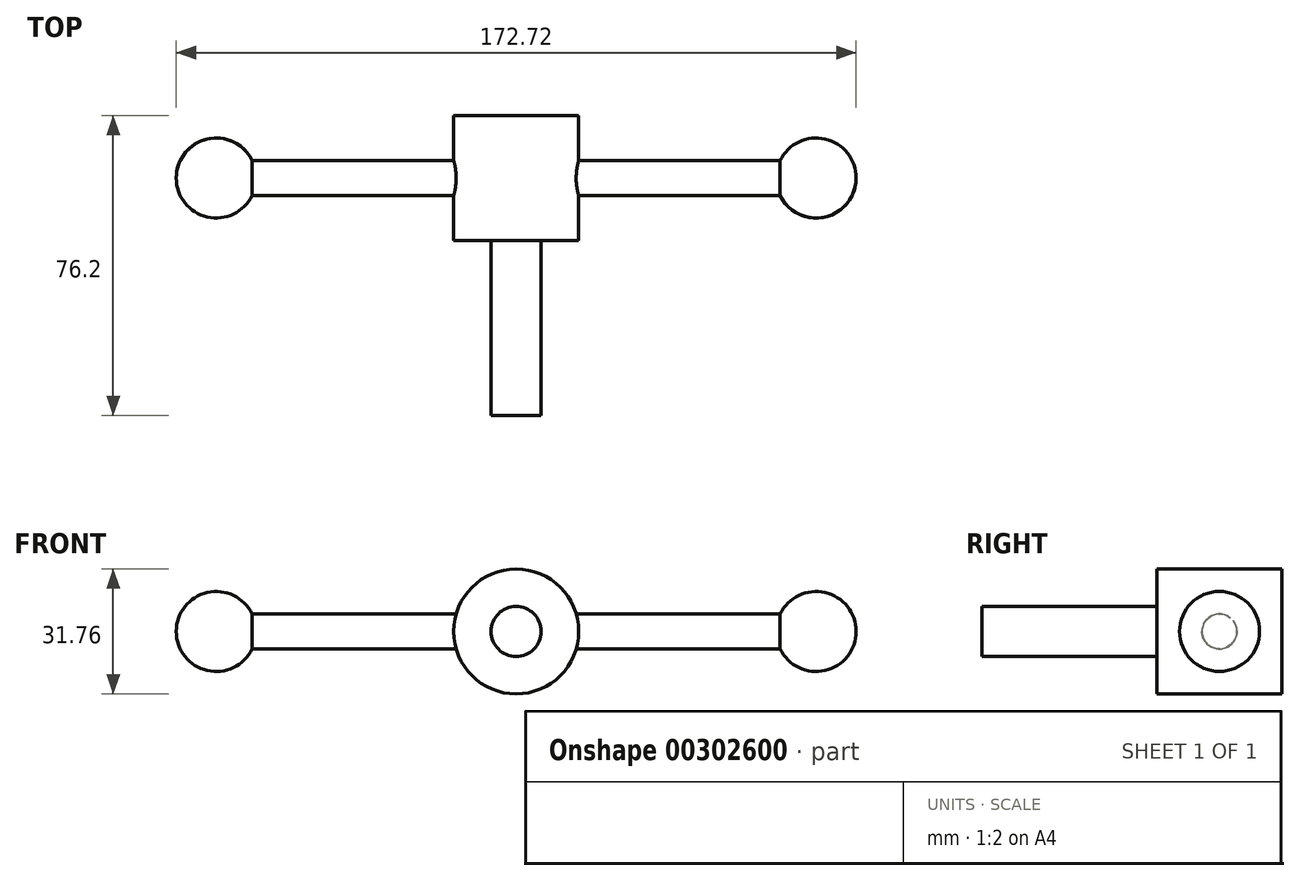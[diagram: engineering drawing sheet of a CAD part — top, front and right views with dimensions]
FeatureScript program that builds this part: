
annotation { "Feature Type Name" : "Feature", "Feature Type Description" : "" }
export const myFeature = defineFeature(function(context is Context, id is Id, definition is map)
    precondition{}
    {
        {
            var Q0;
            Q0=qCreatedBy(makeId("Front.planeOp"),FACE);
            var sketch = newSketch(context, id + "F0", { "sketchPlane" : qUnion([Q0])});
            skCircle(sketch, "E0", {"center": v(0, 0) * mm, "radius": 6.35 * mm});
            skSolve(sketch);
        }
        {
            var Q0;
            Q0=makeQuery(id+"F0.imprint","IMPRINT",FACE,{"disambiguationData":[TD([[makeQuery(id+"F0.imprint","IMPRINT",EDGE,{"derivedFrom":sQuery(id+"F0.wireOp",EDGE,"E0")}),1.0]])]});
            extrude(context, id + "F1", {"entities" : qUnion([Q0]), "depth" : 44.45 * mm});
        }
        {
            var Q0;
            Q0=makeQuery(id+"F1.opExtrude","CAP_FACE",FACE,{"disambiguationData":[OSD([sQuery(id+"F0.wireOp",EDGE,"E0")])],"isStart":true});
            var sketch = newSketch(context, id + "F2", { "sketchPlane" : qUnion([Q0])});
            skCircle(sketch, "E1", {"center": v(0, 0) * mm, "radius": 15.88 * mm});
            skSolve(sketch);
        }
        {
            var Q0;
            Q0=makeQuery(id+"F2.imprint","IMPRINT",FACE,{"disambiguationData":[TD([[makeQuery(id+"F2.imprint","IMPRINT",EDGE,{"derivedFrom":sQuery(id+"F2.wireOp",EDGE,"E1")}),1.0]])]});
            var Q1;
            Q1=makeQuery(id+"F2.imprint","IMPRINT",FACE,{"disambiguationData":[TD([[makeQuery(id+"F2.imprint","IMPRINT",EDGE,{"derivedFrom":makeQuery(id+"F1.opExtrude","CAP_EDGE",EDGE,{"disambiguationData":[OSD([sQuery(id+"F0.wireOp",EDGE,"E0")])],"isStart":true})}),-1.0]])]});
            extrude(context, id + "F3", {"entities" : qUnion([Q0, Q1]), "operationType" : NewBodyOperationType.ADD, "depth" : 31.75 * mm});
        }
        {
            var Q0;
            Q0=qCreatedBy(makeId("Top.planeOp"),FACE);
            var sketch = newSketch(context, id + "F4", { "sketchPlane" : qUnion([Q0])});
            skLineSegment(sketch, "E2", {"start": v(-86.36, 15.88) * mm, "end": v(-66.04, 15.88) * mm});
            skArc(sketch, "E3", {"start": v(-66.04, 15.88) * mm, "mid": v(-76.2, 26.04) * mm, "end": v(-86.36, 15.88) * mm});
            skArc(sketch, "E4", {"start": v(86.36, 15.88) * mm, "mid": v(76.2, 26.04) * mm, "end": v(66.04, 15.88) * mm});
            skLineSegment(sketch, "E5", {"start": v(0, 0) * mm, "end": v(0, 63.62) * mm, "construction": true});
            skLineSegment(sketch, "E6.trimOffspring", {"start": v(66.04, 15.88) * mm, "end": v(86.36, 15.88) * mm});
            skLineSegment(sketch, "E7", {"start": v(-67.06, 20.32) * mm, "end": v(67.06, 20.32) * mm});
            skLineSegment(sketch, "E8", {"start": v(-66.04, 15.88) * mm, "end": v(66.04, 15.88) * mm, "construction": true});
            skLineSegment(sketch, "E9", {"start": v(-66.04, 15.88) * mm, "end": v(66.04, 15.88) * mm});
            skSolve(sketch);
        }
        {
            var Q0;
            {var subQ0=sQuery(id+"F4.wireOp",EDGE,"E2");Q0=makeQuery(id+"F4.imprint","IMPRINT",FACE,{"disambiguationData":[TD([[makeQuery(id+"F4.imprint","IMPRINT",EDGE,{"derivedFrom":subQ0}),1.0]])]});}
            var Q1;
            {var subQ2=sQuery(id+"F4.wireOp",EDGE,"E7");Q1=makeQuery(id+"F4.imprint","IMPRINT",FACE,{"disambiguationData":[TD([[makeQuery(id+"F4.imprint","IMPRINT",EDGE,{"derivedFrom":subQ2}),-1.0]])]});}
            var Q2;
            {var subQ0=sQuery(id+"F4.wireOp",EDGE,"E6.trimOffspring");Q2=makeQuery(id+"F4.imprint","IMPRINT",FACE,{"disambiguationData":[TD([[makeQuery(id+"F4.imprint","IMPRINT",EDGE,{"derivedFrom":subQ0}),1.0]])]});}
            var Q3;
            Q3=sQuery(id+"F4.wireOp",EDGE,"E9");
            revolve(context, id + "F5", {"operationType" : NewBodyOperationType.ADD, "entities" : qUnion([Q0, Q1, Q2]), "axis" : qUnion([Q3]), "revolveType" : RevolveType.FULL});
        }
    });
